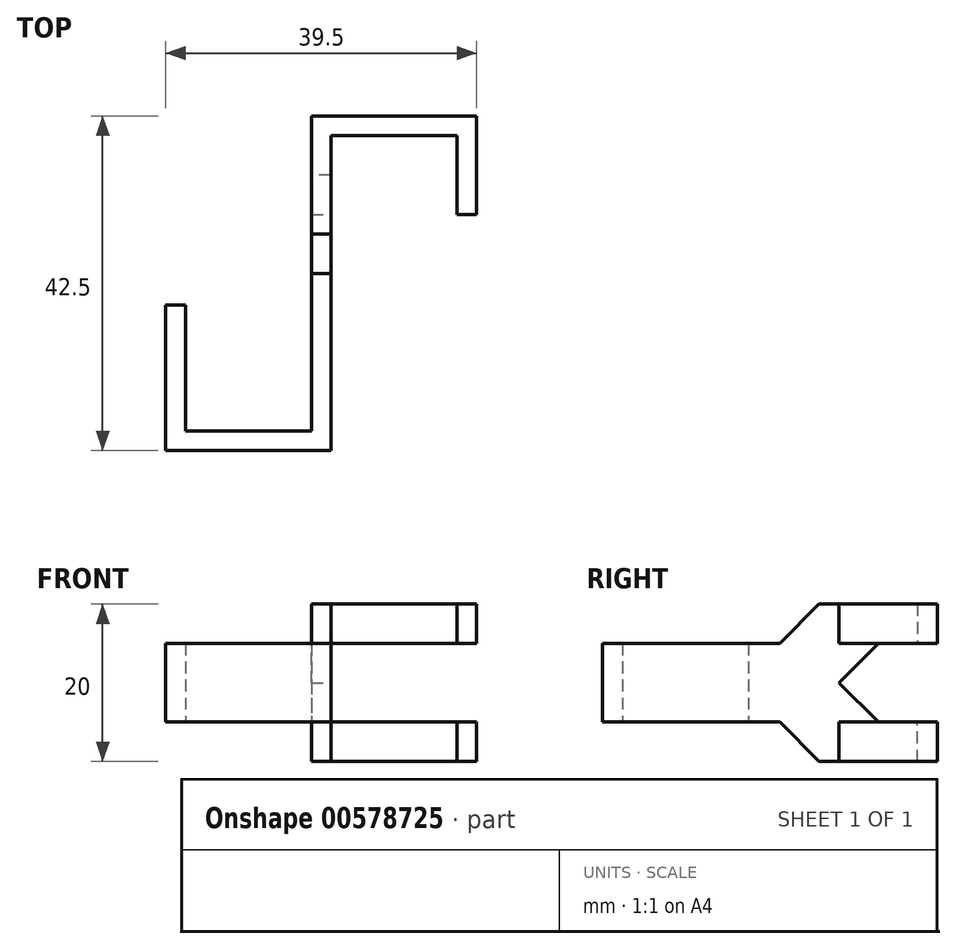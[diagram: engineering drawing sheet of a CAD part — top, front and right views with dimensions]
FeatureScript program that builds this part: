
annotation { "Feature Type Name" : "Feature", "Feature Type Description" : "" }
export const myFeature = defineFeature(function(context is Context, id is Id, definition is map)
    precondition{}
    {
        {
            var Q0;
            Q0=qCreatedBy(makeId("Top.planeOp"),FACE);
            var sketch = newSketch(context, id + "F0", { "sketchPlane" : qUnion([Q0])});
            skLineSegment(sketch, "E0", {"start": v(0, 0) * mm, "end": v(0, 10) * mm});
            skLineSegment(sketch, "E1", {"start": v(0, 10) * mm, "end": v(-16, 10) * mm});
            skLineSegment(sketch, "E2", {"start": v(-16, 10) * mm, "end": v(-16, -30) * mm});
            skLineSegment(sketch, "E3", {"start": v(-16, -30) * mm, "end": v(-37, -30) * mm});
            skLineSegment(sketch, "E4", {"start": v(-37, -30) * mm, "end": v(-37, -11.5) * mm});
            skLineSegment(sketch, "E5", {"start": v(-37, -11.5) * mm, "end": v(-34.5, -11.5) * mm});
            skLineSegment(sketch, "E6", {"start": v(-34.5, -11.5) * mm, "end": v(-34.5, -27.5) * mm});
            skLineSegment(sketch, "E7", {"start": v(-34.5, -27.5) * mm, "end": v(-18.5, -27.5) * mm});
            skLineSegment(sketch, "E8", {"start": v(-18.5, -27.5) * mm, "end": v(-18.5, 12.5) * mm});
            skLineSegment(sketch, "E9", {"start": v(-18.5, 12.5) * mm, "end": v(2.5, 12.5) * mm});
            skLineSegment(sketch, "E10", {"start": v(2.5, 12.5) * mm, "end": v(2.5, 0) * mm});
            skLineSegment(sketch, "E11", {"start": v(2.5, 0) * mm, "end": v(0, 0) * mm});
            skLineSegment(sketch, "E12", {"start": v(-8, 12.5) * mm, "end": v(-8, 10) * mm, "construction": true});
            skLineSegment(sketch, "E13", {"start": v(-18.5, 0) * mm, "end": v(-16, 0) * mm});
            skSolve(sketch);
        }
        {
            var Q0;
            {var subQ0=sQuery(id+"F0.wireOp",EDGE,"E3");Q0=makeQuery(id+"F0.imprint","IMPRINT",FACE,{"disambiguationData":[TD([[makeQuery(id+"F0.imprint","IMPRINT",EDGE,{"derivedFrom":subQ0}),-1.0]])]});}
            extrude(context, id + "F1", {"entities" : qUnion([Q0]), "depth" : 5 * mm, "offsetDistance" : 25 * mm});
        }
        {
            var Q0;
            Q0=makeQuery(id+"F1.opExtrude","CAP_FACE",FACE,{"disambiguationData":[OSD([sQuery(id+"F0.wireOp",EDGE,"E2"),sQuery(id+"F0.wireOp",EDGE,"E3"),sQuery(id+"F0.wireOp",EDGE,"E4"),sQuery(id+"F0.wireOp",EDGE,"E5"),sQuery(id+"F0.wireOp",EDGE,"E6"),sQuery(id+"F0.wireOp",EDGE,"E7"),sQuery(id+"F0.wireOp",EDGE,"E8"),sQuery(id+"F0.wireOp",EDGE,"E13")])],"isStart":false});
            var sketch = newSketch(context, id + "F2", { "sketchPlane" : qUnion([Q0])});
            skLineSegment(sketch, "E14", {"start": v(-18.5, 12.5) * mm, "end": v(2.5, 12.5) * mm});
            skLineSegment(sketch, "E15", {"start": v(2.5, 12.5) * mm, "end": v(2.5, 0) * mm});
            skLineSegment(sketch, "E16", {"start": v(2.5, 0) * mm, "end": v(0, 0) * mm});
            skLineSegment(sketch, "E17", {"start": v(0, 0) * mm, "end": v(0, 10) * mm});
            skLineSegment(sketch, "E18", {"start": v(0, 10) * mm, "end": v(-16, 10) * mm});
            skLineSegment(sketch, "E19", {"start": v(-18.5, -2.5) * mm, "end": v(-16, -2.5) * mm});
            skLineSegment(sketch, "E20", {"start": v(-18.5, 12.5) * mm, "end": v(-18.5, -2.5) * mm});
            skLineSegment(sketch, "E21", {"start": v(-16, -2.5) * mm, "end": v(-16, 10) * mm});
            skSolve(sketch);
        }
        {
            var Q0;
            {var subQ0=sQuery(id+"F2.wireOp",EDGE,"E14");Q0=makeQuery(id+"F2.imprint","IMPRINT",FACE,{"disambiguationData":[TD([[makeQuery(id+"F2.imprint","IMPRINT",EDGE,{"derivedFrom":subQ0}),-1.0]])]});}
            var Q1;
            {var subQ0=sQuery(id+"F2.wireOp",EDGE,"E19");Q1=makeQuery(id+"F2.imprint","IMPRINT",FACE,{"disambiguationData":[TD([[makeQuery(id+"F2.imprint","IMPRINT",EDGE,{"derivedFrom":subQ0}),1.0]])]});}
            extrude(context, id + "F3", {"entities" : qUnion([Q0, Q1]), "operationType" : NewBodyOperationType.ADD, "depth" : 5 * mm, "offsetDistance" : 25 * mm});
        }
        {
            var Q0;
            Q0=makeQuery(id+"F3.boolean.opBoolean","MERGE",FACE,{"derivedFrom":[makeQuery(id+"F1.opExtrude","SWEPT_FACE",FACE,{"disambiguationData":[OSD([sQuery(id+"F0.wireOp",EDGE,"E8")])]}),makeQuery(id+"F3.opExtrude","SWEPT_FACE",FACE,{"disambiguationData":[OSD([sQuery(id+"F2.wireOp",EDGE,"E20")])]})]});
            var sketch = newSketch(context, id + "F4", { "sketchPlane" : qUnion([Q0])});
            skLineSegment(sketch, "E22", {"start": v(2.5, 10) * mm, "end": v(7.5, 5) * mm});
            skLineSegment(sketch, "E23", {"start": v(0, 0) * mm, "end": v(-5, 5) * mm});
            skLineSegment(sketch, "E24", {"start": v(2.5, 10) * mm, "end": v(2.5, 5) * mm});
            skLineSegment(sketch, "E25", {"start": v(2.5, 5) * mm, "end": v(7.5, 5) * mm});
            skLineSegment(sketch, "E26", {"start": v(0, 0) * mm, "end": v(0, 5) * mm});
            skLineSegment(sketch, "E27", {"start": v(0, 5) * mm, "end": v(-5, 5) * mm});
            skSolve(sketch);
        }
        {
            var Q0;
            Q0=makeQuery(id+"F4.imprint","IMPRINT",FACE,{"disambiguationData":[TD([[makeQuery(id+"F4.imprint","IMPRINT",EDGE,{"derivedFrom":sQuery(id+"F4.wireOp",EDGE,"E23")}),-1.0]])]});
            var Q1;
            Q1=makeQuery(id+"F4.imprint","IMPRINT",FACE,{"disambiguationData":[TD([[makeQuery(id+"F4.imprint","IMPRINT",EDGE,{"derivedFrom":sQuery(id+"F4.wireOp",EDGE,"E22")}),-1.0]])]});
            var Q2;
            Q2=makeQuery(id+"F3.boolean.opBoolean","MERGE",FACE,{"derivedFrom":[makeQuery(id+"F1.opExtrude","SWEPT_FACE",FACE,{"disambiguationData":[OSD([sQuery(id+"F0.wireOp",EDGE,"E2")])]}),makeQuery(id+"F3.opExtrude","SWEPT_FACE",FACE,{"disambiguationData":[OSD([sQuery(id+"F2.wireOp",EDGE,"E21")])]})]});
            extrude(context, id + "F5", {"entities" : qUnion([Q0, Q1]), "operationType" : NewBodyOperationType.ADD, "endBound" : BoundingType.UP_TO_SURFACE, "oppositeDirection" : true, "depth" : 25 * mm, "endBoundEntityFace" : qUnion([Q2]), "offsetDistance" : 25 * mm});
        }
        {
            var Q0;
            Q0=makeQuery(id+"F1.opExtrude","SWEPT_BODY",BODY,{"disambiguationData":[OSD([sQuery(id+"F0.wireOp",EDGE,"E2"),sQuery(id+"F0.wireOp",EDGE,"E3"),sQuery(id+"F0.wireOp",EDGE,"E4"),sQuery(id+"F0.wireOp",EDGE,"E5"),sQuery(id+"F0.wireOp",EDGE,"E6"),sQuery(id+"F0.wireOp",EDGE,"E7"),sQuery(id+"F0.wireOp",EDGE,"E8"),sQuery(id+"F0.wireOp",EDGE,"E13")])]});
            var Q1;
            Q1=qCreatedBy(makeId("Top.planeOp"),FACE);
            mirror(context, id + "F6", {"operationType" : NewBodyOperationType.ADD, "entities" : qUnion([Q0]), "mirrorPlane" : qUnion([Q1])});
        }
    });
